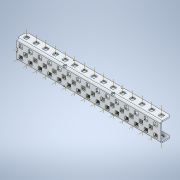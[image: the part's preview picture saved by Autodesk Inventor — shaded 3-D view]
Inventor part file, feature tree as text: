
AUTODESK INVENTOR PART (.ipt)
format: ipt  version: 2020 (Build 240168000, 168)  size: 1,240,064 bytes
history: native  units: in
note: dims shown in document units (in); Inventor stores cm internally (conversion verified against a paired STEP export)
features: other x78, plane x7, pattern_linear x4, split x1, sheet_metal_op x1
ambient origin geometry x8: Origin, YZ Plane, XZ Plane, XY Plane, X Axis, Y Axis, Z Axis, Center Point
bodies: Solid1 (feature_tree)
feature tree (91):
  other  "Work Axis1"
  pattern_linear  "Rectangular Pattern1"  Count1=15 Spacing1=0.5in
  other  "Work Axis72"
  pattern_linear  "Rectangular Pattern2"  Count1=15 Spacing1=0.5in
  pattern_linear  "Rectangular Pattern3"  Count1=15 Spacing1=0.5in
  other  "Work Axis141"
  pattern_linear  "Rectangular Pattern4"  Count1=14 Spacing1=0.5in
  plane  "Work Plane7"
  split  "Split1"
  plane  "Work Plane1"
  plane  "Work Plane2"
  other  "Work Point1"
  other  "Work Axis2"
  other  "Work Axis3"
  other  "Work Axis4"
  other  "Work Axis5"
  other  "Work Axis6"
  other  "Work Axis7"
  other  "Work Axis8"
  other  "Work Axis9"
  other  "Work Axis10"
  other  "Work Axis11"
  other  "Work Axis12"
  other  "Work Axis13"
  other  "Work Axis14"
  other  "Work Axis15"
  other  "Work Axis36"
  other  "Work Axis37"
  other  "Work Axis38"
  other  "Work Axis39"
  other  "Work Axis40"
  other  "Work Axis41"
  other  "Work Axis42"
  other  "Work Axis43"
  other  "Work Axis44"
  other  "Work Axis45"
  other  "Work Axis46"
  other  "Work Axis47"
  other  "Work Axis48"
  other  "Work Axis49"
  other  "Work Axis50"
  plane  "Work Plane3"
  plane  "Work Plane4"
  other  "Work Point2"
  other  "Work Axis71"
  other  "Work Point3"
  other  "Work Axis73"
  other  "Work Axis74"
  other  "Work Axis75"
  other  "Work Axis76"
  other  "Work Axis77"
  other  "Work Axis78"
  other  "Work Axis79"
  other  "Work Axis80"
  other  "Work Axis81"
  other  "Work Axis82"
  other  "Work Axis83"
  other  "Work Axis84"
  other  "Work Axis85"
  other  "Work Axis86"
  other  "Work Axis107"
  other  "Work Axis108"
  other  "Work Axis109"
  other  "Work Axis110"
  plane  "Work Plane5"
  plane  "Work Plane6"
  other  "Work Point4"
  other  "Work Axis142"
  other  "Work Axis143"
  other  "Work Axis144"
  other  "Work Axis145"
  other  "Work Axis146"
  other  "Work Axis147"
  other  "Work Axis148"
  other  "Work Axis149"
  other  "Work Axis150"
  other  "Work Axis151"
  other  "Work Axis152"
  other  "Work Axis153"
  other  "Work Axis154"
  other  "Work Axis175"
  other  "Work Axis176"
  other  "Work Axis177"
  other  "Work Axis178"
  other  "Work Axis179"
  other  "Work Axis180"
  other  "Work Axis181"
  other  "Work Axis182"
  other  "Work Axis183"
  other  "Work Axis184"
  sheet_metal_op  "Fold1"
